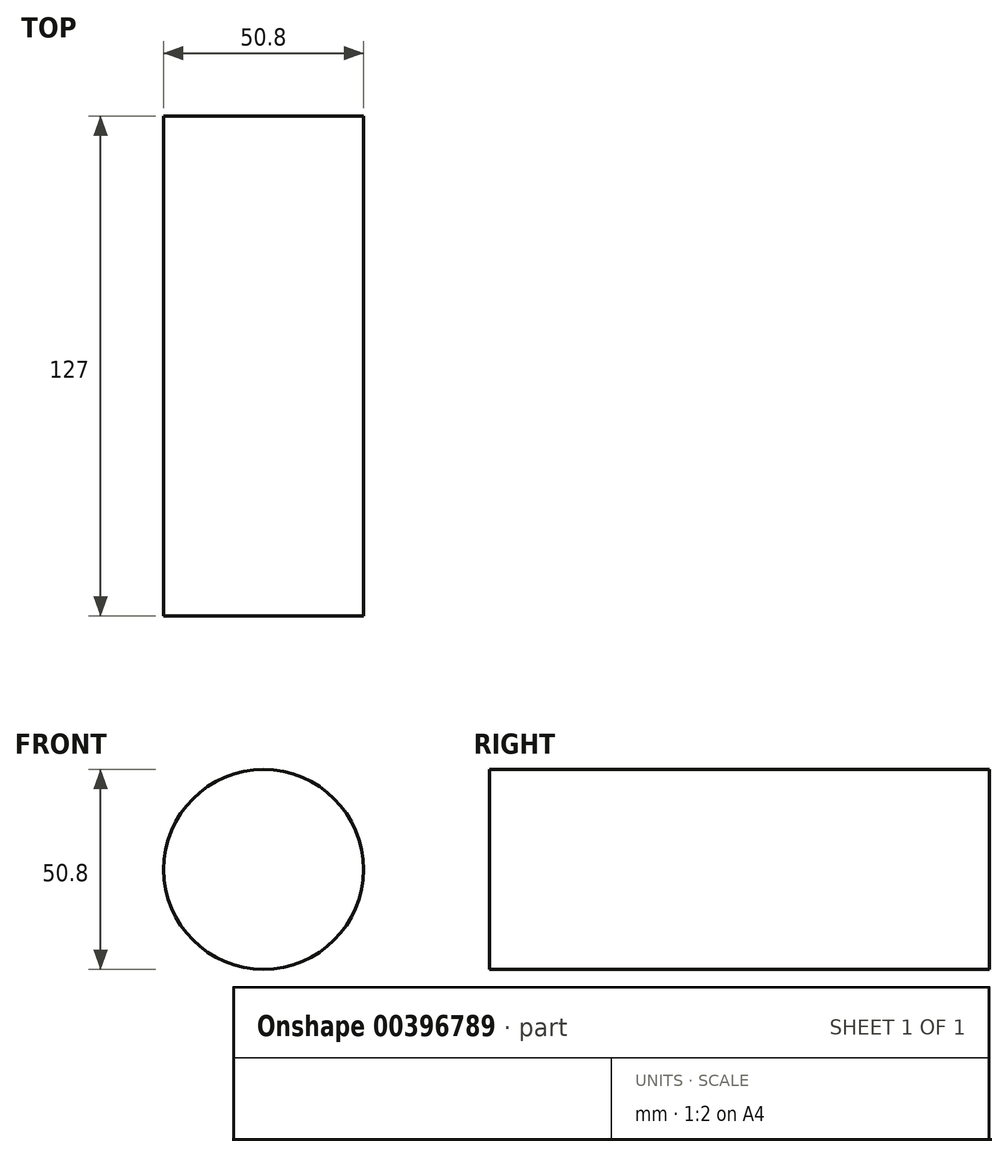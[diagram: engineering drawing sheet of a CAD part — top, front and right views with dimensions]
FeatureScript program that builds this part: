
annotation { "Feature Type Name" : "Feature", "Feature Type Description" : "" }
export const myFeature = defineFeature(function(context is Context, id is Id, definition is map)
    precondition{}
    {
        {
            var Q0;
            Q0=qCreatedBy(makeId("Front.planeOp"),FACE);
            var sketch = newSketch(context, id + "F0", { "sketchPlane" : qUnion([Q0])});
            skCircle(sketch, "E0", {"center": v(0, 0) * mm, "radius": 25.4 * mm});
            skSolve(sketch);
        }
        {
            var Q0;
            Q0 = qSketchRegion(id + "F0", true);
            extrude(context, id + "F1", {"entities" : qUnion([Q0]), "depth" : 101.6 * mm});
        }
        {
            var Q0;
            Q0=qCreatedBy(makeId("Front.planeOp"),FACE);
            var sketch = newSketch(context, id + "F2", { "sketchPlane" : qUnion([Q0])});
            skCircle(sketch, "E1", {"center": v(0, 0) * mm, "radius": 22.23 * mm});
            skSolve(sketch);
        }
        {
            var Q0;
            Q0=makeQuery(id+"F1.opExtrude","CAP_FACE",FACE,{"disambiguationData":[OSD([sQuery(id+"F0.wireOp",EDGE,"E0")])],"isStart":false});
            extrude(context, id + "F3", {"entities" : qUnion([Q0]), "operationType" : NewBodyOperationType.ADD, "depth" : 25.4 * mm});
        }
        {
            var Q0;
            Q0=sQuery(id+"F2.wireOp",EDGE,"E1");
            extrude(context, id + "F4", {"bodyType" : ToolBodyType.SURFACE, "surfaceEntities" : qUnion([Q0]), "depth" : 25.4 * mm});
        }
    });
